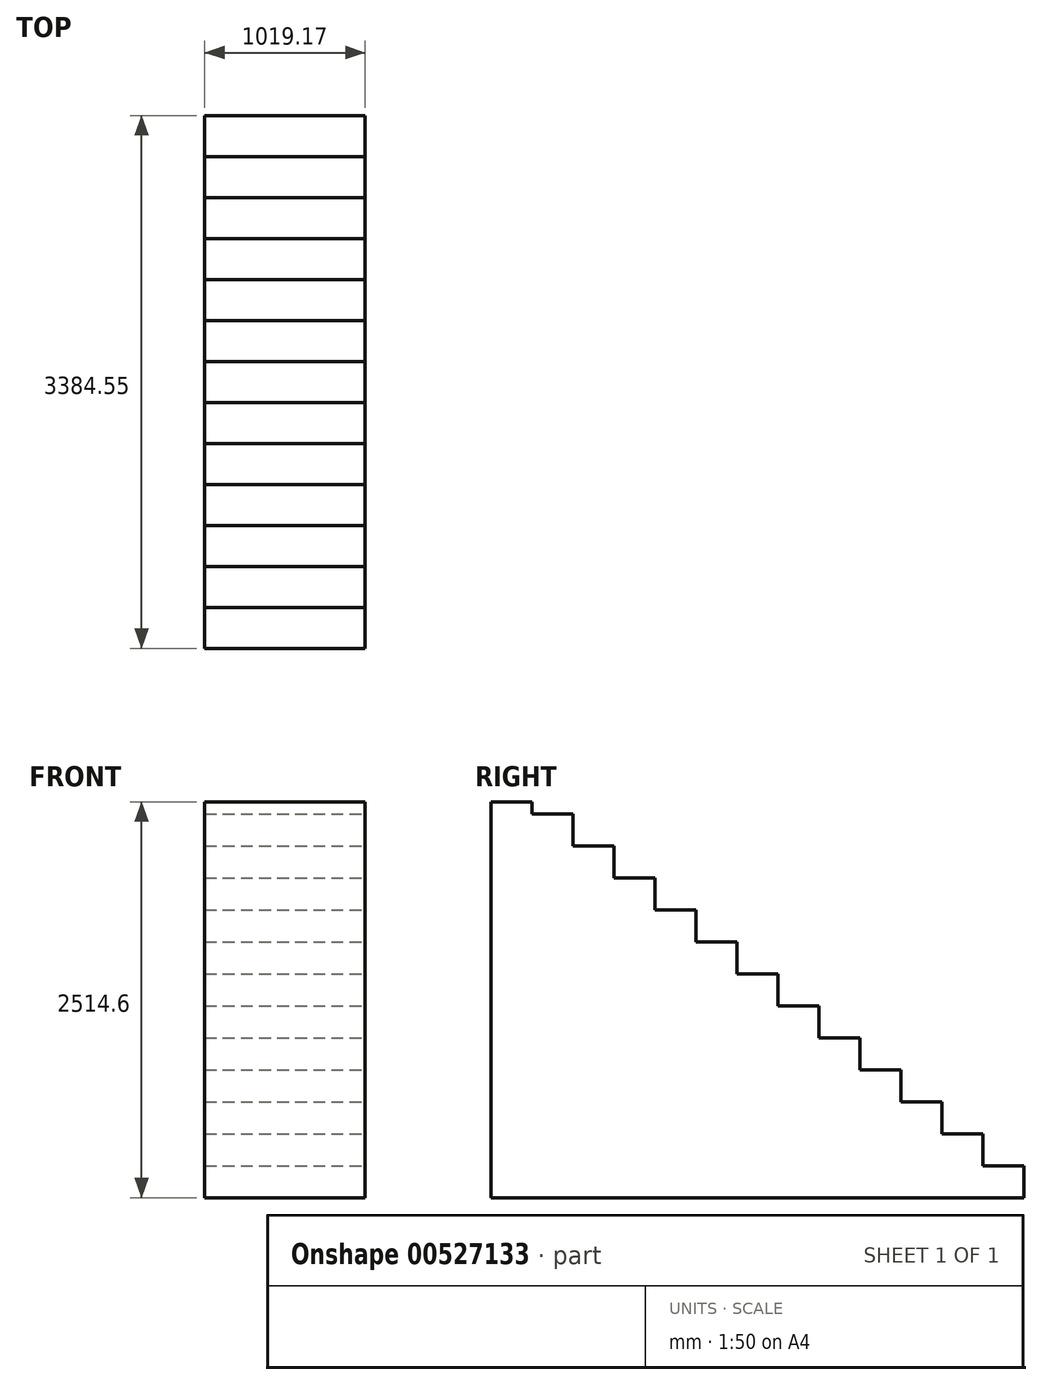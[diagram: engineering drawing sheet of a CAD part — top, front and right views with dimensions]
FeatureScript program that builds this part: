
annotation { "Feature Type Name" : "Feature", "Feature Type Description" : "" }
export const myFeature = defineFeature(function(context is Context, id is Id, definition is map)
    precondition{}
    {
        {
            var Q0;
            Q0=qCreatedBy(makeId("Top.planeOp"),FACE);
            var sketch = newSketch(context, id + "F0", { "sketchPlane" : qUnion([Q0])});
            skLineSegment(sketch, "E0.bottom", {"start": v(0, 0) * mm, "end": v(1019.18, 0) * mm});
            skLineSegment(sketch, "E0.top", {"start": v(0, 3384.55) * mm, "end": v(1019.17, 3384.55) * mm});
            skLineSegment(sketch, "E0.left", {"start": v(0, 0) * mm, "end": v(0, 3384.55) * mm});
            skLineSegment(sketch, "E0.right", {"start": v(1019.18, 0) * mm, "end": v(1019.18, 3384.55) * mm});
            skSolve(sketch);
        }
        {
            var Q0;
            Q0=makeQuery(id+"F0.imprint","IMPRINT",FACE,{"disambiguationData":[TD([[makeQuery(id+"F0.imprint","IMPRINT",EDGE,{"derivedFrom":sQuery(id+"F0.wireOp",EDGE,"E0.bottom")}),1.0]])]});
            extrude(context, id + "F1", {"entities" : qUnion([Q0]), "depth" : 2514.6 * mm, "offsetDistance" : 25.4 * mm});
        }
        {
            var Q0;
            Q0=makeQuery(id+"F1.opExtrude","SWEPT_FACE",FACE,{"disambiguationData":[OSD([sQuery(id+"F0.wireOp",EDGE,"E0.right")])]});
            var sketch = newSketch(context, id + "F2", { "sketchPlane" : qUnion([Q0])});
            skLineSegment(sketch, "E1", {"start": v(3384.55, 0) * mm, "end": v(3384.55, 203.2) * mm});
            skLineSegment(sketch, "E2", {"start": v(3384.55, 203.2) * mm, "end": v(3124.2, 203.2) * mm});
            skLineSegment(sketch, "E3", {"start": v(3124.2, 203.2) * mm, "end": v(3124.2, 406.4) * mm});
            skLineSegment(sketch, "E4", {"start": v(3124.2, 406.4) * mm, "end": v(2863.85, 406.4) * mm});
            skLineSegment(sketch, "E5", {"start": v(2863.85, 406.4) * mm, "end": v(2863.85, 609.6) * mm});
            skLineSegment(sketch, "E6", {"start": v(2863.85, 609.6) * mm, "end": v(2603.5, 609.6) * mm});
            skLineSegment(sketch, "E7", {"start": v(2603.5, 609.6) * mm, "end": v(2603.5, 812.8) * mm});
            skLineSegment(sketch, "E8", {"start": v(2603.5, 812.8) * mm, "end": v(2343.15, 812.8) * mm});
            skLineSegment(sketch, "E9", {"start": v(2343.15, 812.8) * mm, "end": v(2343.15, 1016) * mm});
            skLineSegment(sketch, "E10", {"start": v(2343.15, 1016) * mm, "end": v(2082.8, 1016) * mm});
            skLineSegment(sketch, "E11", {"start": v(2082.8, 1016) * mm, "end": v(2082.8, 1219.2) * mm});
            skLineSegment(sketch, "E12", {"start": v(2082.8, 1219.2) * mm, "end": v(1822.45, 1219.2) * mm});
            skLineSegment(sketch, "E13", {"start": v(1822.45, 1219.2) * mm, "end": v(1822.45, 1422.4) * mm});
            skLineSegment(sketch, "E14", {"start": v(1822.45, 1422.4) * mm, "end": v(1562.1, 1422.4) * mm});
            skLineSegment(sketch, "E15", {"start": v(1562.1, 1422.4) * mm, "end": v(1562.1, 1625.6) * mm});
            skLineSegment(sketch, "E16", {"start": v(1562.1, 1625.6) * mm, "end": v(1301.75, 1625.6) * mm});
            skLineSegment(sketch, "E17", {"start": v(1301.75, 1625.6) * mm, "end": v(1301.75, 1828.8) * mm});
            skLineSegment(sketch, "E18", {"start": v(1301.75, 1828.8) * mm, "end": v(1041.4, 1828.8) * mm});
            skLineSegment(sketch, "E19", {"start": v(1041.4, 1828.8) * mm, "end": v(1041.4, 2032) * mm});
            skLineSegment(sketch, "E20", {"start": v(1041.4, 2032) * mm, "end": v(781.05, 2032) * mm});
            skLineSegment(sketch, "E21", {"start": v(781.05, 2032) * mm, "end": v(781.05, 2235.2) * mm});
            skLineSegment(sketch, "E22", {"start": v(781.05, 2235.2) * mm, "end": v(520.7, 2235.2) * mm});
            skLineSegment(sketch, "E23", {"start": v(520.7, 2235.2) * mm, "end": v(520.7, 2438.4) * mm});
            skLineSegment(sketch, "E24", {"start": v(520.7, 2438.4) * mm, "end": v(260.35, 2438.4) * mm});
            skLineSegment(sketch, "E25", {"start": v(260.35, 2438.4) * mm, "end": v(260.35, 2641.6) * mm});
            skLineSegment(sketch, "E26", {"start": v(260.35, 2641.6) * mm, "end": v(0, 2641.6) * mm});
            skLineSegment(sketch, "E27", {"start": v(0, 2641.6) * mm, "end": v(0, 2844.8) * mm});
            skLineSegment(sketch, "E28", {"start": v(0, 2844.8) * mm, "end": v(-260.35, 2844.8) * mm});
            skSolve(sketch);
        }
        {
            var Q0;
            {var subQ0=sQuery(id+"F2.wireOp",EDGE,"E2");Q0=makeQuery(id+"F2.imprint","IMPRINT",FACE,{"disambiguationData":[TD([[makeQuery(id+"F2.imprint","IMPRINT",EDGE,{"derivedFrom":subQ0}),-1.0]])]});}
            extrude(context, id + "F3", {"entities" : qUnion([Q0]), "operationType" : NewBodyOperationType.REMOVE, "oppositeDirection" : true, "depth" : 1019.17 * mm, "offsetDistance" : 25.4 * mm});
        }
    });
